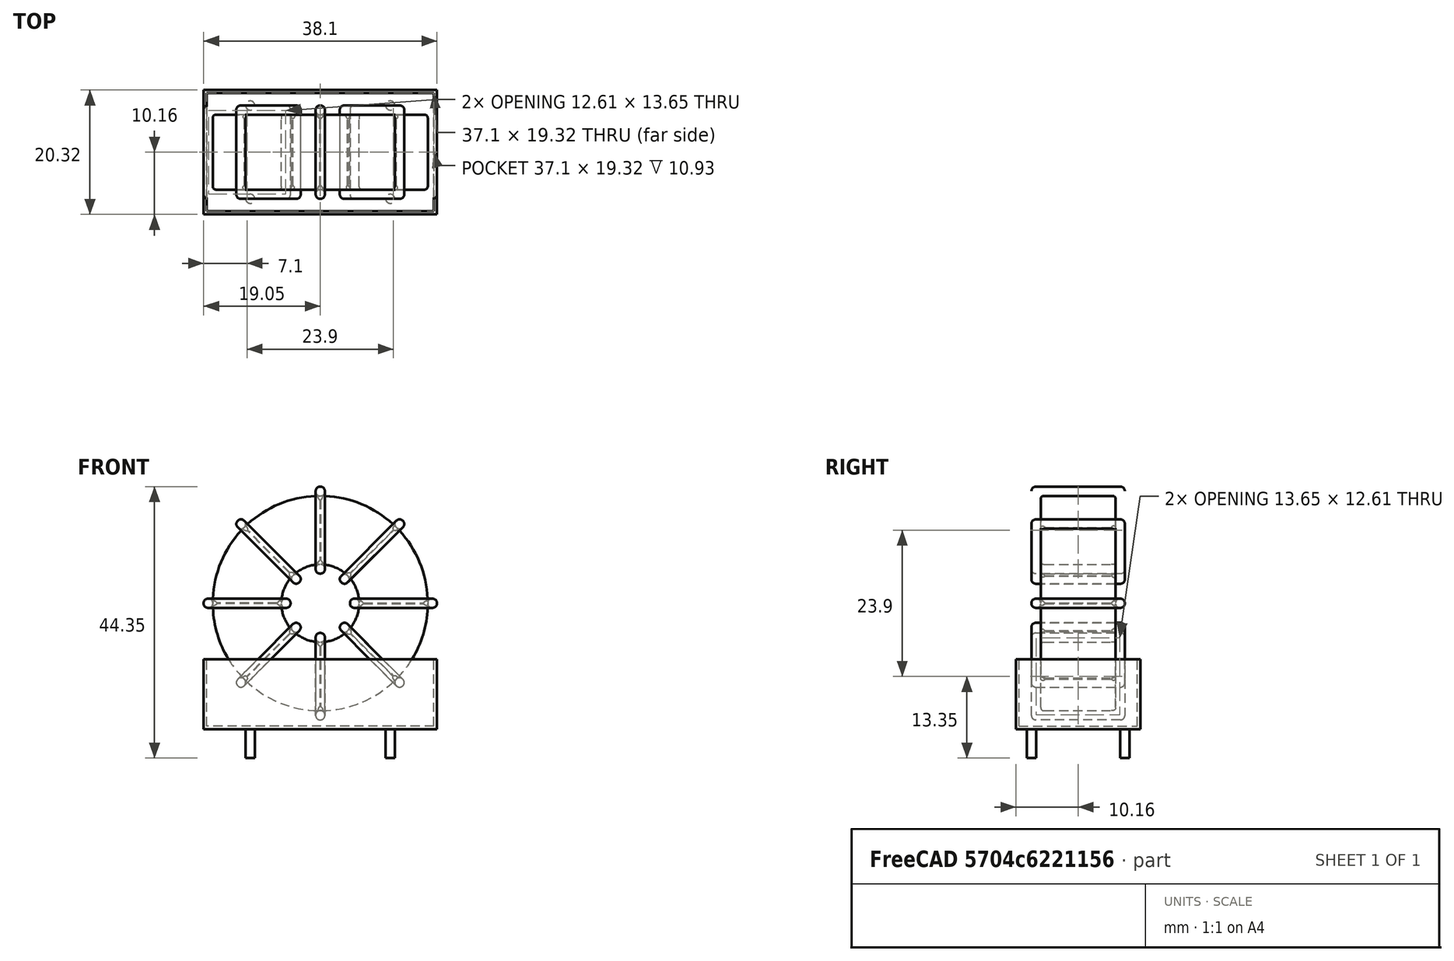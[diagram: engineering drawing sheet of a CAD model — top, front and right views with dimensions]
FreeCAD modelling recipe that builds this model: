
FCSTD DOCUMENT  (FreeCAD 0.16R6712 (Git))
Label: L_CommonMode_Toroid_Vertical_L38.1mm_W20.3mm_Px15.24mm_Py22.86mm_Bourns_8100
License: All rights reserved
LicenseURL: http://en.wikipedia.org/wiki/All_rights_reserved
objects: Sketcher::SketchObject×8, PartDesign::Pad×8, PartDesign::Fillet×5, Spreadsheet::Sheet×1, Part::MultiFuse×1
note: 30 computed .brp shape members not serialized (recipe doc carries the construction recipe); baked Part::Feature solids carry a one-line shape summary decoded from their .brp

FEATURE [Spreadsheet::Sheet] Spreadsheet  label="dimensions"
  cells = A1=Wx; B1(Wx)=38.09999999999999; C1(WW)=12.7; D1(iWx)=38.09999999999999; A2=Wy; B2(Wy)=15.24; D2(iWy)=20.32; A3=RM; B3(RMx)=15.24; C3(RMy)=22.86; A4=d_wire; B4(d_wire)=1.5; A5=H; B5(H)=31; A6=offsetx; B6(offsetx)=7.619999999999997
FEATURE [Sketcher::SketchObject] Sketch
  Placement = pos=(11.43,-7.62,0) rot=(1,0,0;1.5708rad)
  expr: Placement.Base.x = Spreadsheet.RMy / 2
  expr: Constraints[4] = Spreadsheet.WW / 2
  expr: Placement.Base.y = -Spreadsheet.RMx / 2
  expr: Constraints[0] = Spreadsheet.Wx / 2 - Spreadsheet.d_wire
  expr: Constraints[2] = Spreadsheet.Wx / 2 + Spreadsheet.d_wire + 0.5
  sketch-geometry (2):
    g0: Circle CenterX=0 CenterY=21.05 CenterZ=0 NormalX=0 NormalY=0 NormalZ=1 Radius=17.55
    g1: Circle CenterX=0 CenterY=21.05 CenterZ=0 NormalX=0 NormalY=0 NormalZ=1 Radius=6.35
  constraints (5):
    c: Radius(g0) = 17.55
    c: DistanceX(g-1,g0) = 0
    c: DistanceY(g-1,g0) = 21.05
    c: Coincident(g1,g0)
    c: Radius(g1) = 6.35
FEATURE [PartDesign::Pad] Pad
  Length = 12.24
  Length2 = 100
  Midplane = true
  Placement = pos=(11.43,-7.62,0) rot=(1,0,0;1.5708rad)
  Sketch = -> Sketch
  Type = 0
  expr: Length = Spreadsheet.Wy - 2 * Spreadsheet.d_wire
FEATURE [Sketcher::SketchObject] Sketch001
  Placement = pos=(0,0,0.75) rot=(0,0,1;0rad)
  expr: Constraints[4] = Spreadsheet.RMy
  expr: Constraints[2] = -Spreadsheet.RMx
  expr: Constraints[1] = Spreadsheet.d_wire / 2
  sketch-geometry (4):
    g0: Circle CenterX=0 CenterY=0 CenterZ=0 NormalX=0 NormalY=0 NormalZ=1 Radius=0.75
    g1: Circle CenterX=22.86 CenterY=-15.24 CenterZ=0 NormalX=0 NormalY=0 NormalZ=1 Radius=0.75
    g2: Circle CenterX=0 CenterY=-15.24 CenterZ=0 NormalX=0 NormalY=0 NormalZ=1 Radius=0.75
    g3: Circle CenterX=22.86 CenterY=0 CenterZ=0 NormalX=0 NormalY=0 NormalZ=1 Radius=0.75
  constraints (11):
    c: Equal(g0,g1)
    c: Radius(g0) = 0.75
    c: DistanceY(g-1,g1) = -15.24
    c: Coincident(g0,g-1)
    c: DistanceX(g-1,g1) = 22.86
    c: PointOnObject(g2,g-2)
    c: DistanceY(g-1,g3) = 0
    c: DistanceY(g2,g1) = 0
    c: DistanceX(g3,g1) = 0
    c: Equal(g3,g2)
    c: Equal(g2,g1)
FEATURE [PartDesign::Pad] Pad001
  Length = 5
  Length2 = 0
  Placement = pos=(0,0,0.75) rot=(0,0,1;0rad)
  Reversed = true
  Sketch = -> Sketch001
  Type = 0
FEATURE [PartDesign::Fillet] Fillet
  Base = -> Pad [Edge6,Edge3,Edge2]
  Placement = pos=(11.43,-7.62,0) rot=(1,0,0;1.5708rad)
  Radius = 0.5
FEATURE [Sketcher::SketchObject] Sketch003
  Placement = pos=(11.43,0,21.05) rot=(1,0,0;3.14159rad)
  expr: Placement.Base.x = Spreadsheet.RMy / 2
  expr: Constraints[18] = Spreadsheet.d_wire
  expr: Constraints[16] = Spreadsheet.d_wire
  expr: Constraints[19] = Spreadsheet.d_wire
  expr: Constraints[17] = Spreadsheet.d_wire
  expr: Placement.Base.y = -1 * (Spreadsheet.RMx - Spreadsheet.Wy) / 2
  expr: Constraints[21] = (Spreadsheet.Wx - Spreadsheet.WW) / 2 - Spreadsheet.d_wire
  expr: Constraints[22] = Spreadsheet.Wx / 2 - Spreadsheet.d_wire
  expr: Constraints[43] = Spreadsheet.d_wire
  expr: Constraints[48] = Spreadsheet.Wx - Spreadsheet.d_wire * 2
  expr: Constraints[49] = Spreadsheet.Wy
  expr: Placement.Base.z = Spreadsheet.Wx / 2 + Spreadsheet.d_wire + 0.5
  sketch-geometry (16):
    g0: LineSegment StartX=-4.85 StartY=0 StartZ=0 EndX=-19.05 EndY=0 EndZ=0
    g1: LineSegment StartX=-19.05 StartY=0 StartZ=0 EndX=-19.05 EndY=15.24 EndZ=0
    g2: LineSegment StartX=-19.05 StartY=15.24 StartZ=0 EndX=-4.85 EndY=15.24 EndZ=0
    g3: LineSegment StartX=-4.85 StartY=15.24 StartZ=0 EndX=-4.85 EndY=0 EndZ=0
    g4: LineSegment StartX=-17.55 StartY=13.74 StartZ=0 EndX=-6.35 EndY=13.74 EndZ=0
    g5: LineSegment StartX=-6.35 StartY=13.74 StartZ=0 EndX=-6.35 EndY=1.5 EndZ=0
    g6: LineSegment StartX=-6.35 StartY=1.5 StartZ=0 EndX=-17.55 EndY=1.5 EndZ=0
    g7: LineSegment StartX=-17.55 StartY=1.5 StartZ=0 EndX=-17.55 EndY=13.74 EndZ=0
    g8: LineSegment StartX=4.85 StartY=15.24 StartZ=0 EndX=19.05 EndY=15.24 EndZ=0
    g9: LineSegment StartX=19.05 StartY=15.24 StartZ=0 EndX=19.05 EndY=0 EndZ=0
    g10: LineSegment StartX=19.05 StartY=0 StartZ=0 EndX=4.85 EndY=0 EndZ=0
    g11: LineSegment StartX=4.85 StartY=0 StartZ=0 EndX=4.85 EndY=15.24 EndZ=0
    g12: LineSegment StartX=6.35 StartY=13.74 StartZ=0 EndX=17.55 EndY=13.74 EndZ=0
    g13: LineSegment StartX=17.55 StartY=13.74 StartZ=0 EndX=17.55 EndY=1.5 EndZ=0
    g14: LineSegment StartX=17.55 StartY=1.5 StartZ=0 EndX=6.35 EndY=1.5 EndZ=0
    g15: LineSegment StartX=6.35 StartY=1.5 StartZ=0 EndX=6.35 EndY=13.74 EndZ=0
  constraints (50):
    c: Horizontal(g0)
    c: Coincident(g1,g0)
    c: Vertical(g1)
    c: Coincident(g2,g1)
    c: Horizontal(g2)
    c: Coincident(g3,g2)
    c: Coincident(g3,g0)
    c: Vertical(g3)
    c: Coincident(g4,g5)
    c: Coincident(g5,g6)
    c: Coincident(g6,g7)
    c: Coincident(g7,g4)
    c: Horizontal(g4)
    c: Horizontal(g6)
    c: Vertical(g5)
    c: Vertical(g7)
    c: DistanceX(g1,g4) = 1.5
    c: DistanceY(g4,g1) = 1.5
    c: DistanceX(g5,g0) = 1.5
    c: DistanceY(g0,g5) = 1.5
    c: DistanceY(g-1,g0) = 0
    c: DistanceX(g6,g6) = 11.2
    c: DistanceX(g6,g-1) = 17.55
    c: Coincident(g8,g9)
    c: Coincident(g9,g10)
    c: Coincident(g10,g11)
    c: Coincident(g11,g8)
    c: Horizontal(g8)
    c: Horizontal(g10)
    c: Vertical(g9)
    c: Vertical(g11)
    c: Coincident(g12,g13)
    c: Coincident(g13,g14)
    c: Coincident(g14,g15)
    c: Coincident(g15,g12)
    c: Horizontal(g12)
    c: Horizontal(g14)
    c: Vertical(g13)
    c: Vertical(g15)
    c: DistanceY(g8,g2) = 0
    c: DistanceY(g10,g0) = 0
    c: DistanceY(g14,g5) = 0
    c: DistanceY(g12,g4) = 0
    c: DistanceX(g8,g12) = 1.5
    c: Equal(g8,g2)
    c: Equal(g12,g4)
    c: Equal(g9,g1)
    c: Equal(g13,g7)
    c: DistanceX(g4,g12) = 35.1
    c: DistanceY(g0,g1) = 15.24
FEATURE [PartDesign::Pad] Pad002
  Length = 1.5
  Length2 = 100
  Midplane = true
  Placement = pos=(11.43,0,21.05) rot=(1,0,0;3.14159rad)
  Sketch = -> Sketch003
  Type = 0
  expr: Length = Spreadsheet.d_wire
FEATURE [PartDesign::Fillet] Fillet001
  Base = -> Pad002 [Edge38,Edge41,Edge42,Edge43,Edge29,Edge32,Edge33,Edge34,Edge25,Edge35,Edge36,Edge13,Edge14,Edge15,Edge16,Edge17,Edge18,Edge19,Edge1,Edge2,Edge3,Edge4,Edge5,Edge6,Edge7,Edge37,Edge39,Edge40,Edge20,Edge23,Edge24,Edge21,Edge22,Edge8,Edge9,Edge10,Edge11,Edge12,Edge26,Edge27,+8 more]
  Placement = pos=(11.43,0,21.05) rot=(1,0,0;3.14159rad)
  Radius = 0.705
  expr: Radius = Spreadsheet.d_wire * 0.47
FEATURE [Sketcher::SketchObject] Sketch004
  Placement = pos=(11.43,0,21.05) rot=(0.92388,0,0.382683;3.14159rad)
  expr: Placement.Base.x = Spreadsheet.RMy / 2
  expr: Constraints[18] = Spreadsheet.d_wire
  expr: Constraints[16] = Spreadsheet.d_wire
  expr: Constraints[19] = Spreadsheet.d_wire
  expr: Constraints[17] = Spreadsheet.d_wire
  expr: Placement.Base.y = -1 * (Spreadsheet.RMx - Spreadsheet.Wy) / 2
  expr: Constraints[21] = (Spreadsheet.Wx - Spreadsheet.WW) / 2 - Spreadsheet.d_wire
  expr: Constraints[22] = Spreadsheet.Wx / 2 - Spreadsheet.d_wire
  expr: Constraints[43] = Spreadsheet.d_wire
  expr: Constraints[48] = Spreadsheet.Wx - 2 * Spreadsheet.d_wire
  expr: Constraints[49] = Spreadsheet.Wy
  expr: Placement.Base.z = Spreadsheet.Wx / 2 + Spreadsheet.d_wire + 0.5
  sketch-geometry (16):
    g0: LineSegment StartX=-4.85 StartY=0 StartZ=0 EndX=-19.05 EndY=0 EndZ=0
    g1: LineSegment StartX=-19.05 StartY=0 StartZ=0 EndX=-19.05 EndY=15.24 EndZ=0
    g2: LineSegment StartX=-19.05 StartY=15.24 StartZ=0 EndX=-4.85 EndY=15.24 EndZ=0
    g3: LineSegment StartX=-4.85 StartY=15.24 StartZ=0 EndX=-4.85 EndY=0 EndZ=0
    g4: LineSegment StartX=-17.55 StartY=13.74 StartZ=0 EndX=-6.35 EndY=13.74 EndZ=0
    g5: LineSegment StartX=-6.35 StartY=13.74 StartZ=0 EndX=-6.35 EndY=1.5 EndZ=0
    g6: LineSegment StartX=-6.35 StartY=1.5 StartZ=0 EndX=-17.55 EndY=1.5 EndZ=0
    g7: LineSegment StartX=-17.55 StartY=1.5 StartZ=0 EndX=-17.55 EndY=13.74 EndZ=0
    g8: LineSegment StartX=4.85 StartY=15.24 StartZ=0 EndX=19.05 EndY=15.24 EndZ=0
    g9: LineSegment StartX=19.05 StartY=15.24 StartZ=0 EndX=19.05 EndY=0 EndZ=0
    g10: LineSegment StartX=19.05 StartY=0 StartZ=0 EndX=4.85 EndY=0 EndZ=0
    g11: LineSegment StartX=4.85 StartY=0 StartZ=0 EndX=4.85 EndY=15.24 EndZ=0
    g12: LineSegment StartX=6.35 StartY=13.74 StartZ=0 EndX=17.55 EndY=13.74 EndZ=0
    g13: LineSegment StartX=17.55 StartY=13.74 StartZ=0 EndX=17.55 EndY=1.5 EndZ=0
    g14: LineSegment StartX=17.55 StartY=1.5 StartZ=0 EndX=6.35 EndY=1.5 EndZ=0
    g15: LineSegment StartX=6.35 StartY=1.5 StartZ=0 EndX=6.35 EndY=13.74 EndZ=0
  constraints (50):
    c: Horizontal(g0)
    c: Coincident(g1,g0)
    c: Vertical(g1)
    c: Coincident(g2,g1)
    c: Horizontal(g2)
    c: Coincident(g3,g2)
    c: Coincident(g3,g0)
    c: Vertical(g3)
    c: Coincident(g4,g5)
    c: Coincident(g5,g6)
    c: Coincident(g6,g7)
    c: Coincident(g7,g4)
    c: Horizontal(g4)
    c: Horizontal(g6)
    c: Vertical(g5)
    c: Vertical(g7)
    c: DistanceX(g1,g4) = 1.5
    c: DistanceY(g4,g1) = 1.5
    c: DistanceX(g5,g0) = 1.5
    c: DistanceY(g0,g5) = 1.5
    c: DistanceY(g-1,g0) = 0
    c: DistanceX(g6,g6) = 11.2
    c: DistanceX(g6,g-1) = 17.55
    c: Coincident(g8,g9)
    c: Coincident(g9,g10)
    c: Coincident(g10,g11)
    c: Coincident(g11,g8)
    c: Horizontal(g8)
    c: Horizontal(g10)
    c: Vertical(g9)
    c: Vertical(g11)
    c: Coincident(g12,g13)
    c: Coincident(g13,g14)
    c: Coincident(g14,g15)
    c: Coincident(g15,g12)
    c: Horizontal(g12)
    c: Horizontal(g14)
    c: Vertical(g13)
    c: Vertical(g15)
    c: DistanceY(g8,g2) = 0
    c: DistanceY(g10,g0) = 0
    c: DistanceY(g14,g5) = 0
    c: DistanceY(g12,g4) = 0
    c: DistanceX(g8,g12) = 1.5
    c: Equal(g8,g2)
    c: Equal(g12,g4)
    c: Equal(g9,g1)
    c: Equal(g13,g7)
    c: DistanceX(g4,g12) = 35.1
    c: DistanceY(g0,g1) = 15.24
FEATURE [PartDesign::Pad] Pad003
  Length = 1.5
  Length2 = 100
  Midplane = true
  Placement = pos=(11.43,0,21.05) rot=(0.92388,0,0.382683;3.14159rad)
  Sketch = -> Sketch004
  Type = 0
  expr: Length = Spreadsheet.d_wire
FEATURE [PartDesign::Fillet] Fillet002
  Base = -> Pad003 [Edge38,Edge41,Edge42,Edge43,Edge29,Edge32,Edge33,Edge34,Edge25,Edge35,Edge36,Edge13,Edge14,Edge15,Edge16,Edge17,Edge18,Edge19,Edge1,Edge2,Edge3,Edge4,Edge5,Edge6,Edge7,Edge37,Edge39,Edge40,Edge20,Edge23,Edge24,Edge21,Edge22,Edge8,Edge9,Edge10,Edge11,Edge12,Edge26,Edge27,+8 more]
  Placement = pos=(11.43,0,21.05) rot=(0.92388,0,0.382683;3.14159rad)
  Radius = 0.705
  expr: Radius = Spreadsheet.d_wire * 0.47
FEATURE [Sketcher::SketchObject] Sketch005
  Placement = pos=(11.43,0,21.05) rot=(0.92388,0,-0.382683;3.14159rad)
  expr: Placement.Base.x = Spreadsheet.RMy / 2
  expr: Constraints[18] = Spreadsheet.d_wire
  expr: Constraints[16] = Spreadsheet.d_wire
  expr: Constraints[19] = Spreadsheet.d_wire
  expr: Constraints[17] = Spreadsheet.d_wire
  expr: Placement.Base.y = -1 * (Spreadsheet.RMx - Spreadsheet.Wy) / 2
  expr: Constraints[21] = (Spreadsheet.Wx - Spreadsheet.WW) / 2 - Spreadsheet.d_wire
  expr: Constraints[22] = Spreadsheet.Wx / 2 - Spreadsheet.d_wire
  expr: Constraints[43] = Spreadsheet.d_wire
  expr: Constraints[48] = Spreadsheet.Wx - 2 * Spreadsheet.d_wire
  expr: Constraints[49] = Spreadsheet.Wy
  expr: Placement.Base.z = Spreadsheet.Wx / 2 + Spreadsheet.d_wire + 0.5
  sketch-geometry (16):
    g0: LineSegment StartX=-4.85 StartY=0 StartZ=0 EndX=-19.05 EndY=0 EndZ=0
    g1: LineSegment StartX=-19.05 StartY=0 StartZ=0 EndX=-19.05 EndY=15.24 EndZ=0
    g2: LineSegment StartX=-19.05 StartY=15.24 StartZ=0 EndX=-4.85 EndY=15.24 EndZ=0
    g3: LineSegment StartX=-4.85 StartY=15.24 StartZ=0 EndX=-4.85 EndY=0 EndZ=0
    g4: LineSegment StartX=-17.55 StartY=13.74 StartZ=0 EndX=-6.35 EndY=13.74 EndZ=0
    g5: LineSegment StartX=-6.35 StartY=13.74 StartZ=0 EndX=-6.35 EndY=1.5 EndZ=0
    g6: LineSegment StartX=-6.35 StartY=1.5 StartZ=0 EndX=-17.55 EndY=1.5 EndZ=0
    g7: LineSegment StartX=-17.55 StartY=1.5 StartZ=0 EndX=-17.55 EndY=13.74 EndZ=0
    g8: LineSegment StartX=4.85 StartY=15.24 StartZ=0 EndX=19.05 EndY=15.24 EndZ=0
    g9: LineSegment StartX=19.05 StartY=15.24 StartZ=0 EndX=19.05 EndY=0 EndZ=0
    g10: LineSegment StartX=19.05 StartY=0 StartZ=0 EndX=4.85 EndY=0 EndZ=0
    g11: LineSegment StartX=4.85 StartY=0 StartZ=0 EndX=4.85 EndY=15.24 EndZ=0
    g12: LineSegment StartX=6.35 StartY=13.74 StartZ=0 EndX=17.55 EndY=13.74 EndZ=0
    g13: LineSegment StartX=17.55 StartY=13.74 StartZ=0 EndX=17.55 EndY=1.5 EndZ=0
    g14: LineSegment StartX=17.55 StartY=1.5 StartZ=0 EndX=6.35 EndY=1.5 EndZ=0
    g15: LineSegment StartX=6.35 StartY=1.5 StartZ=0 EndX=6.35 EndY=13.74 EndZ=0
  constraints (50):
    c: Horizontal(g0)
    c: Coincident(g1,g0)
    c: Vertical(g1)
    c: Coincident(g2,g1)
    c: Horizontal(g2)
    c: Coincident(g3,g2)
    c: Coincident(g3,g0)
    c: Vertical(g3)
    c: Coincident(g4,g5)
    c: Coincident(g5,g6)
    c: Coincident(g6,g7)
    c: Coincident(g7,g4)
    c: Horizontal(g4)
    c: Horizontal(g6)
    c: Vertical(g5)
    c: Vertical(g7)
    c: DistanceX(g1,g4) = 1.5
    c: DistanceY(g4,g1) = 1.5
    c: DistanceX(g5,g0) = 1.5
    c: DistanceY(g0,g5) = 1.5
    c: DistanceY(g-1,g0) = 0
    c: DistanceX(g6,g6) = 11.2
    c: DistanceX(g6,g-1) = 17.55
    c: Coincident(g8,g9)
    c: Coincident(g9,g10)
    c: Coincident(g10,g11)
    c: Coincident(g11,g8)
    c: Horizontal(g8)
    c: Horizontal(g10)
    c: Vertical(g9)
    c: Vertical(g11)
    c: Coincident(g12,g13)
    c: Coincident(g13,g14)
    c: Coincident(g14,g15)
    c: Coincident(g15,g12)
    c: Horizontal(g12)
    c: Horizontal(g14)
    c: Vertical(g13)
    c: Vertical(g15)
    c: DistanceY(g8,g2) = 0
    c: DistanceY(g10,g0) = 0
    c: DistanceY(g14,g5) = 0
    c: DistanceY(g12,g4) = 0
    c: DistanceX(g8,g12) = 1.5
    c: Equal(g8,g2)
    c: Equal(g12,g4)
    c: Equal(g9,g1)
    c: Equal(g13,g7)
    c: DistanceX(g4,g12) = 35.1
    c: DistanceY(g0,g1) = 15.24
FEATURE [PartDesign::Pad] Pad004
  Length = 1.5
  Length2 = 100
  Midplane = true
  Placement = pos=(11.43,0,21.05) rot=(0.92388,0,-0.382683;3.14159rad)
  Sketch = -> Sketch005
  Type = 0
  expr: Length = Spreadsheet.d_wire
FEATURE [PartDesign::Fillet] Fillet003
  Base = -> Pad004 [Edge38,Edge41,Edge42,Edge43,Edge29,Edge32,Edge33,Edge34,Edge25,Edge35,Edge36,Edge13,Edge14,Edge15,Edge16,Edge17,Edge18,Edge19,Edge1,Edge2,Edge3,Edge4,Edge5,Edge6,Edge7,Edge37,Edge39,Edge40,Edge20,Edge23,Edge24,Edge21,Edge22,Edge8,Edge9,Edge10,Edge11,Edge12,Edge26,Edge27,+8 more]
  Placement = pos=(11.43,0,21.05) rot=(0.92388,0,-0.382683;3.14159rad)
  Radius = 0.705
  expr: Radius = Spreadsheet.d_wire * 0.47
FEATURE [Sketcher::SketchObject] Sketch006
  Placement = pos=(11.43,0,21.05) rot=(0.707107,0,0.707107;3.14159rad)
  expr: Placement.Base.x = Spreadsheet.RMy / 2
  expr: Constraints[18] = Spreadsheet.d_wire
  expr: Constraints[16] = Spreadsheet.d_wire
  expr: Constraints[19] = Spreadsheet.d_wire
  expr: Constraints[17] = Spreadsheet.d_wire
  expr: Placement.Base.y = -1 * (Spreadsheet.RMx - Spreadsheet.Wy) / 2
  expr: Constraints[21] = (Spreadsheet.Wx - Spreadsheet.WW) / 2 - Spreadsheet.d_wire
  expr: Constraints[22] = Spreadsheet.Wx / 2 - Spreadsheet.d_wire
  expr: Constraints[43] = Spreadsheet.d_wire
  expr: Constraints[48] = Spreadsheet.Wx - Spreadsheet.d_wire * 2
  expr: Constraints[49] = Spreadsheet.Wy
  expr: Placement.Base.z = Spreadsheet.Wx / 2 + Spreadsheet.d_wire + 0.5
  sketch-geometry (16):
    g0: LineSegment StartX=-4.85 StartY=0 StartZ=0 EndX=-19.05 EndY=0 EndZ=0
    g1: LineSegment StartX=-19.05 StartY=0 StartZ=0 EndX=-19.05 EndY=15.24 EndZ=0
    g2: LineSegment StartX=-19.05 StartY=15.24 StartZ=0 EndX=-4.85 EndY=15.24 EndZ=0
    g3: LineSegment StartX=-4.85 StartY=15.24 StartZ=0 EndX=-4.85 EndY=0 EndZ=0
    g4: LineSegment StartX=-17.55 StartY=13.74 StartZ=0 EndX=-6.35 EndY=13.74 EndZ=0
    g5: LineSegment StartX=-6.35 StartY=13.74 StartZ=0 EndX=-6.35 EndY=1.5 EndZ=0
    g6: LineSegment StartX=-6.35 StartY=1.5 StartZ=0 EndX=-17.55 EndY=1.5 EndZ=0
    g7: LineSegment StartX=-17.55 StartY=1.5 StartZ=0 EndX=-17.55 EndY=13.74 EndZ=0
    g8: LineSegment StartX=4.85 StartY=15.24 StartZ=0 EndX=19.05 EndY=15.24 EndZ=0
    g9: LineSegment StartX=19.05 StartY=15.24 StartZ=0 EndX=19.05 EndY=0 EndZ=0
    g10: LineSegment StartX=19.05 StartY=0 StartZ=0 EndX=4.85 EndY=0 EndZ=0
    g11: LineSegment StartX=4.85 StartY=0 StartZ=0 EndX=4.85 EndY=15.24 EndZ=0
    g12: LineSegment StartX=6.35 StartY=13.74 StartZ=0 EndX=17.55 EndY=13.74 EndZ=0
    g13: LineSegment StartX=17.55 StartY=13.74 StartZ=0 EndX=17.55 EndY=1.5 EndZ=0
    g14: LineSegment StartX=17.55 StartY=1.5 StartZ=0 EndX=6.35 EndY=1.5 EndZ=0
    g15: LineSegment StartX=6.35 StartY=1.5 StartZ=0 EndX=6.35 EndY=13.74 EndZ=0
  constraints (50):
    c: Horizontal(g0)
    c: Coincident(g1,g0)
    c: Vertical(g1)
    c: Coincident(g2,g1)
    c: Horizontal(g2)
    c: Coincident(g3,g2)
    c: Coincident(g3,g0)
    c: Vertical(g3)
    c: Coincident(g4,g5)
    c: Coincident(g5,g6)
    c: Coincident(g6,g7)
    c: Coincident(g7,g4)
    c: Horizontal(g4)
    c: Horizontal(g6)
    c: Vertical(g5)
    c: Vertical(g7)
    c: DistanceX(g1,g4) = 1.5
    c: DistanceY(g4,g1) = 1.5
    c: DistanceX(g5,g0) = 1.5
    c: DistanceY(g0,g5) = 1.5
    c: DistanceY(g-1,g0) = 0
    c: DistanceX(g6,g6) = 11.2
    c: DistanceX(g6,g-1) = 17.55
    c: Coincident(g8,g9)
    c: Coincident(g9,g10)
    c: Coincident(g10,g11)
    c: Coincident(g11,g8)
    c: Horizontal(g8)
    c: Horizontal(g10)
    c: Vertical(g9)
    c: Vertical(g11)
    c: Coincident(g12,g13)
    c: Coincident(g13,g14)
    c: Coincident(g14,g15)
    c: Coincident(g15,g12)
    c: Horizontal(g12)
    c: Horizontal(g14)
    c: Vertical(g13)
    c: Vertical(g15)
    c: DistanceY(g8,g2) = 0
    c: DistanceY(g10,g0) = 0
    c: DistanceY(g14,g5) = 0
    c: DistanceY(g12,g4) = 0
    c: DistanceX(g8,g12) = 1.5
    c: Equal(g8,g2)
    c: Equal(g12,g4)
    c: Equal(g9,g1)
    c: Equal(g13,g7)
    c: DistanceX(g4,g12) = 35.1
    c: DistanceY(g0,g1) = 15.24
FEATURE [PartDesign::Pad] Pad005
  Length = 1.5
  Length2 = 100
  Midplane = true
  Placement = pos=(11.43,0,21.05) rot=(0.707107,0,0.707107;3.14159rad)
  Sketch = -> Sketch006
  Type = 0
  expr: Length = Spreadsheet.d_wire
FEATURE [PartDesign::Fillet] Fillet004
  Base = -> Pad005 [Edge38,Edge41,Edge42,Edge43,Edge29,Edge32,Edge33,Edge34,Edge25,Edge35,Edge36,Edge13,Edge14,Edge15,Edge16,Edge17,Edge18,Edge19,Edge1,Edge2,Edge3,Edge4,Edge5,Edge6,Edge7,Edge37,Edge39,Edge40,Edge20,Edge23,Edge24,Edge21,Edge22,Edge8,Edge9,Edge10,Edge11,Edge12,Edge26,Edge27,+8 more]
  Placement = pos=(11.43,0,21.05) rot=(0.707107,0,0.707107;3.14159rad)
  Radius = 0.705
  expr: Radius = Spreadsheet.d_wire * 0.47
FEATURE [Sketcher::SketchObject] Sketch007
  Placement = pos=(11.43,0,0.5) rot=(0,0,1;0rad)
  expr: Placement.Base.x = Spreadsheet.RMy / 2
  expr: Placement.Base.z = 0.5
  expr: Constraints[11] = Spreadsheet.iWx / 2
  expr: Constraints[10] = (Spreadsheet.iWy - Spreadsheet.RMx) / 2
  expr: Constraints[9] = Spreadsheet.iWy
  expr: Constraints[8] = Spreadsheet.iWx
  sketch-geometry (4):
    g0: LineSegment StartX=-19.05 StartY=2.54 StartZ=0 EndX=19.05 EndY=2.54 EndZ=0
    g1: LineSegment StartX=19.05 StartY=2.54 StartZ=0 EndX=19.05 EndY=-17.78 EndZ=0
    g2: LineSegment StartX=19.05 StartY=-17.78 StartZ=0 EndX=-19.05 EndY=-17.78 EndZ=0
    g3: LineSegment StartX=-19.05 StartY=-17.78 StartZ=0 EndX=-19.05 EndY=2.54 EndZ=0
  constraints (12):
    c: Coincident(g0,g1)
    c: Coincident(g1,g2)
    c: Coincident(g2,g3)
    c: Coincident(g3,g0)
    c: Horizontal(g0)
    c: Horizontal(g2)
    c: Vertical(g1)
    c: Vertical(g3)
    c: DistanceX(g0,g0) = 38.1
    c: DistanceY(g3,g3) = 20.32
    c: DistanceY(g-1,g0) = 2.54
    c: DistanceX(g0,g-1) = 19.05
FEATURE [PartDesign::Pad] Pad006
  Length = 0.5
  Length2 = 100
  Placement = pos=(11.43,0,0.5) rot=(0,0,1;0rad)
  Sketch = -> Sketch007
  Type = 0
FEATURE [Sketcher::SketchObject] Sketch008
  Placement = pos=(11.43,0,0.5) rot=(0,0,1;0rad)
  expr: Placement.Base.x = Spreadsheet.RMy / 2
  expr: Constraints[8] = Spreadsheet.iWx
  expr: Constraints[9] = Spreadsheet.iWy
  expr: Constraints[10] = (Spreadsheet.iWy - Spreadsheet.RMx) / 2
  expr: Placement.Base.z = 0.5
  expr: Constraints[21] = 0.5
  expr: Constraints[11] = Spreadsheet.iWx / 2
  sketch-geometry (8):
    g0: LineSegment StartX=-19.05 StartY=2.54 StartZ=0 EndX=19.05 EndY=2.54 EndZ=0
    g1: LineSegment StartX=19.05 StartY=2.54 StartZ=0 EndX=19.05 EndY=-17.78 EndZ=0
    g2: LineSegment StartX=19.05 StartY=-17.78 StartZ=0 EndX=-19.05 EndY=-17.78 EndZ=0
    g3: LineSegment StartX=-19.05 StartY=-17.78 StartZ=0 EndX=-19.05 EndY=2.54 EndZ=0
    g4: LineSegment StartX=-18.55 StartY=2.04 StartZ=0 EndX=18.55 EndY=2.04 EndZ=0
    g5: LineSegment StartX=18.55 StartY=2.04 StartZ=0 EndX=18.55 EndY=-17.28 EndZ=0
    g6: LineSegment StartX=18.55 StartY=-17.28 StartZ=0 EndX=-18.55 EndY=-17.28 EndZ=0
    g7: LineSegment StartX=-18.55 StartY=-17.28 StartZ=0 EndX=-18.55 EndY=2.04 EndZ=0
  constraints (24):
    c: Coincident(g0,g1)
    c: Coincident(g1,g2)
    c: Coincident(g2,g3)
    c: Coincident(g3,g0)
    c: Horizontal(g0)
    c: Horizontal(g2)
    c: Vertical(g1)
    c: Vertical(g3)
    c: DistanceX(g0,g0) = 38.1
    c: DistanceY(g3,g3) = 20.32
    c: DistanceY(g-1,g0) = 2.54
    c: DistanceX(g0,g-1) = 19.05
    c: Coincident(g4,g5)
    c: Coincident(g5,g6)
    c: Coincident(g6,g7)
    c: Coincident(g7,g4)
    c: Horizontal(g4)
    c: Horizontal(g6)
    c: Vertical(g5)
    c: Vertical(g7)
    c: DistanceX(g5,g1) = 0.5
    c: DistanceY(g1,g5) = 0.5
    c: DistanceX(g0,g4) = 0.5
    c: DistanceY(g4,g0) = 0.5
FEATURE [PartDesign::Pad] Pad007
  Length = 11.43
  Length2 = 100
  Placement = pos=(11.43,0,0.5) rot=(0,0,1;0rad)
  Sketch = -> Sketch008
  Type = 0
  expr: Length = Spreadsheet.Wx * 0.3
FEATURE [Part::MultiFuse] Pad001_mp_cp  label="L_CommonMode_Toroid_Vertical_L38.1mm_W20.3mm_Px15.24mm_Py22.86mm_Bourns_8100"
  Shapes = -> [Pad001,Fillet,Fillet001,Fillet002,Fillet003,Fillet004,Pad006,Pad007]
